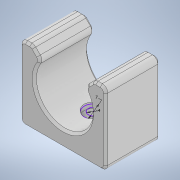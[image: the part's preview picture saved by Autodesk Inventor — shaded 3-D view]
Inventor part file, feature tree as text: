
AUTODESK INVENTOR PART (.ipt)
format: ipt  version: 2020.3 (Build 243373000, 373)  size: 398,336 bytes
history: native  units: mm
features: extrude x3, sketch x2, chamfer x2, fillet x1
ambient origin geometry x8: Origin, YZ Plane, XZ Plane, XY Plane, X Axis, Y Axis, Z Axis, Center Point
bodies: Solid1 (feature_tree)
feature tree (8):
  extrude  "Extrusion1"  Depth=10.5mm
  sketch  "Sketch2"  dims[d2=45.0deg d3=15.75mm d4=21.0mm d5=6.0mm d6=20.0mm d7=0.0mm d8=7.0mm d9=4.0mm d10=10.0mm d11=5.0mm d12=0.0mm d13=0.0mm d14=10.0mm d15=3.0mm d16=0.0mm d17=0.0mm d18=1.5mm d19=2.0mm d20=45.0deg d21=2.0mm d22=0.8mm d23=2.0mm d24=45.0deg]
  extrude  "Extrusion2"  Depth=2.0mm
  extrude  "Extrusion3"  Depth=2.0mm
  chamfer  "Chamfer1"  Distance=6.0mm
  fillet  "Fillet1"  Radius=20.0mm
  chamfer  "Chamfer2"  Distance=7.0mm
  sketch  "Sketch1"  dims[d0=10.5mm d1=17.5mm]
